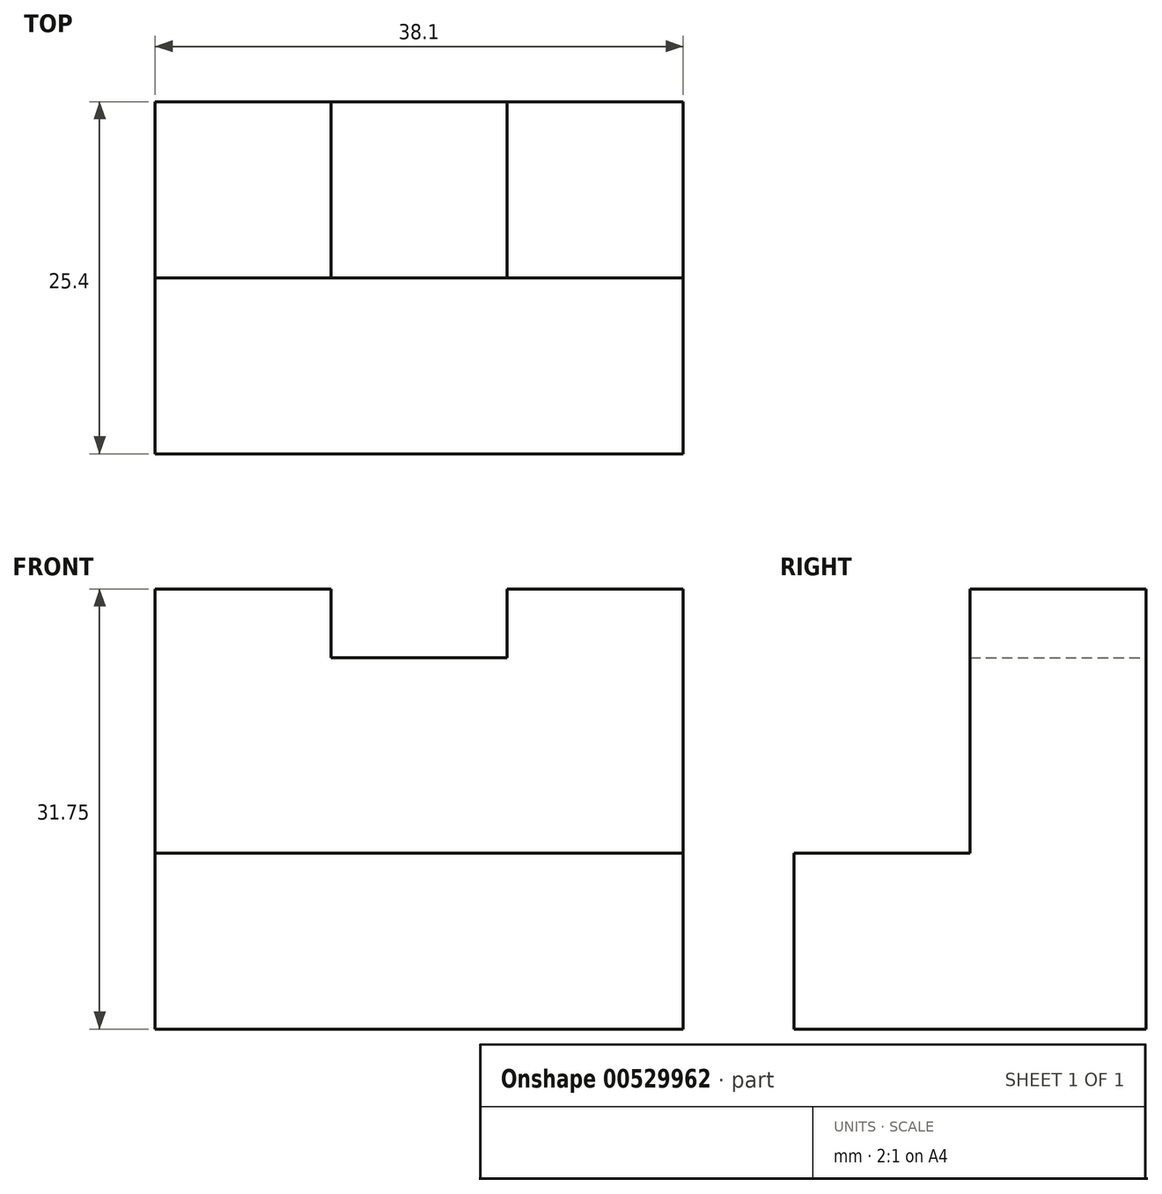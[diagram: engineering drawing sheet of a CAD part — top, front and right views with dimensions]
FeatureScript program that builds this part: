
annotation { "Feature Type Name" : "Feature", "Feature Type Description" : "" }
export const myFeature = defineFeature(function(context is Context, id is Id, definition is map)
    precondition{}
    {
        {
            var Q0;
            Q0=qCreatedBy(makeId("Front.planeOp"),FACE);
            var sketch = newSketch(context, id + "F0", { "sketchPlane" : qUnion([Q0])});
            skLineSegment(sketch, "E0", {"start": v(-39.88, 38.13) * mm, "end": v(-27.18, 38.13) * mm});
            skLineSegment(sketch, "E1", {"start": v(-27.18, 38.13) * mm, "end": v(-27.18, 33.17) * mm});
            skLineSegment(sketch, "E2", {"start": v(-27.18, 33.17) * mm, "end": v(-14.48, 33.17) * mm});
            skLineSegment(sketch, "E3", {"start": v(-14.48, 33.17) * mm, "end": v(-14.48, 38.13) * mm});
            skLineSegment(sketch, "E4", {"start": v(-14.48, 38.13) * mm, "end": v(-1.78, 38.13) * mm});
            skLineSegment(sketch, "E5", {"start": v(-1.78, 38.13) * mm, "end": v(-1.78, 6.38) * mm});
            skLineSegment(sketch, "E6", {"start": v(-1.78, 6.38) * mm, "end": v(-39.88, 6.38) * mm});
            skLineSegment(sketch, "E7", {"start": v(-39.88, 6.38) * mm, "end": v(-39.88, 38.13) * mm});
            skLineSegment(sketch, "E8", {"start": v(-39.88, 19.08) * mm, "end": v(-1.78, 19.08) * mm});
            skSolve(sketch);
        }
        {
            var Q0;
            {var subQ0=sQuery(id+"F0.wireOp",EDGE,"E6");Q0=makeQuery(id+"F0.imprint","IMPRINT",FACE,{"disambiguationData":[TD([[makeQuery(id+"F0.imprint","IMPRINT",EDGE,{"derivedFrom":subQ0}),-1.0]])]});}
            extrude(context, id + "F1", {"entities" : qUnion([Q0]), "depth" : 25.4 * mm, "offsetDistance" : 25.4 * mm});
        }
        {
            var Q0;
            Q0 = qSketchRegion(id + "F0", true);
            extrude(context, id + "F2", {"entities" : qUnion([Q0]), "operationType" : NewBodyOperationType.ADD, "depth" : 12.7 * mm, "offsetDistance" : 25.4 * mm});
        }
    });
